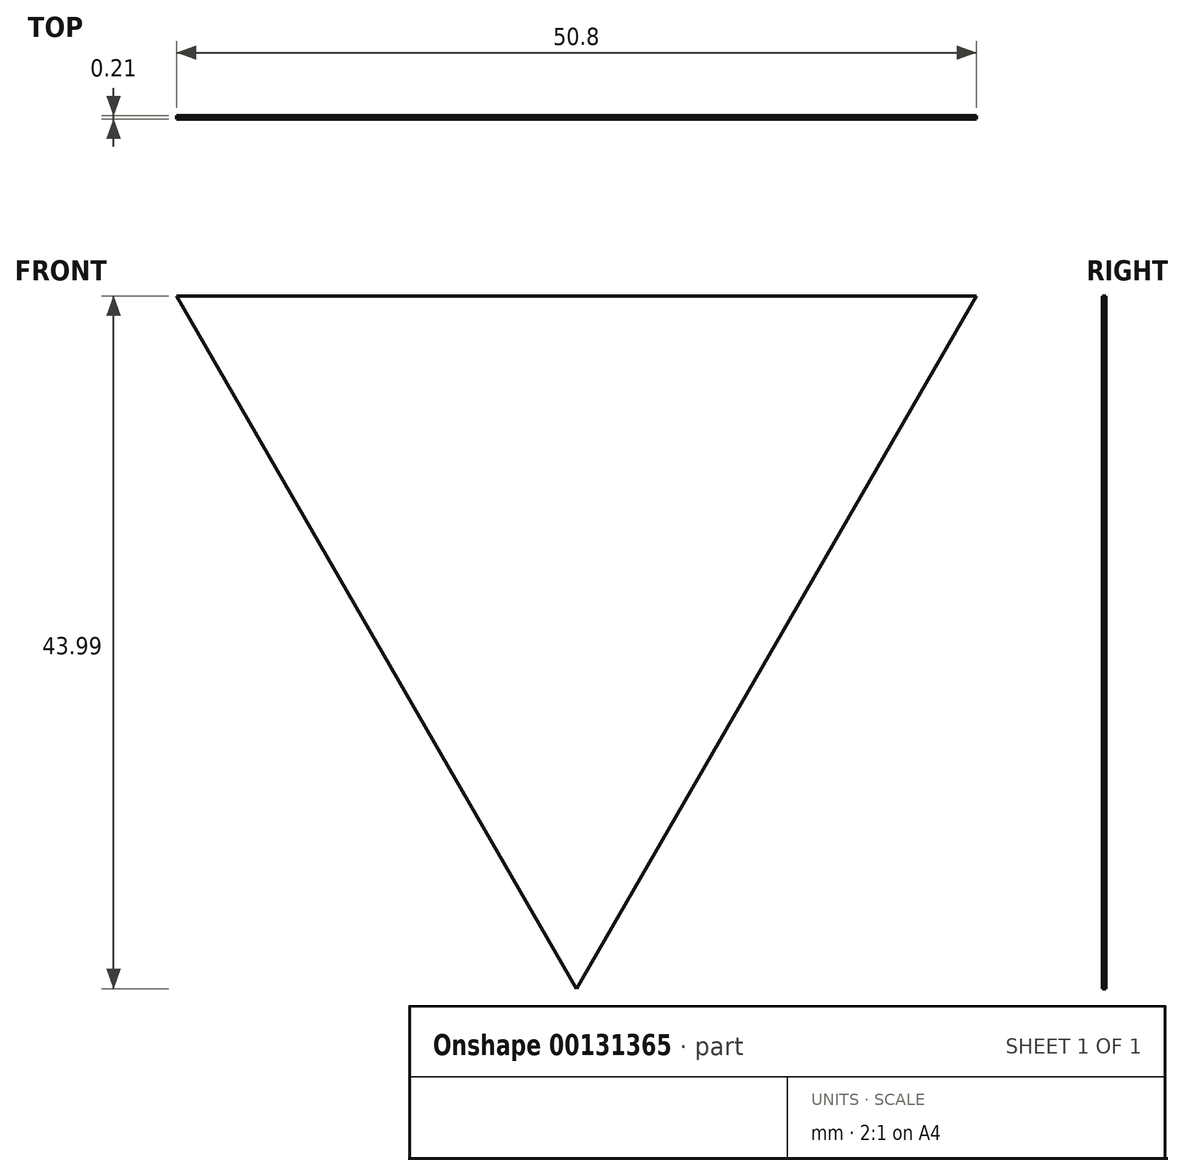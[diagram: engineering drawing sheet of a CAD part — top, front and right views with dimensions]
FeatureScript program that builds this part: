
annotation { "Feature Type Name" : "Feature", "Feature Type Description" : "" }
export const myFeature = defineFeature(function(context is Context, id is Id, definition is map)
    precondition{}
    {
        {
            var Q0;
            Q0=qCreatedBy(makeId("Front.planeOp"),FACE);
            var sketch = newSketch(context, id + "F0", { "sketchPlane" : qUnion([Q0])});
            skLineSegment(sketch, "E0", {"start": v(-25.4, 0) * mm, "end": v(25.4, 0) * mm});
            skLineSegment(sketch, "E1", {"start": v(25.4, 0) * mm, "end": v(0, -44) * mm});
            skLineSegment(sketch, "E2", {"start": v(0, -44) * mm, "end": v(-25.4, 0) * mm});
            skSolve(sketch);
        }
        {
            var Q0;
            Q0 = qSketchRegion(id + "F0", true);
            extrude(context, id + "F1", {"entities" : qUnion([Q0]), "oppositeDirection" : true, "depth" : 0.2 * mm});
        }
    });
